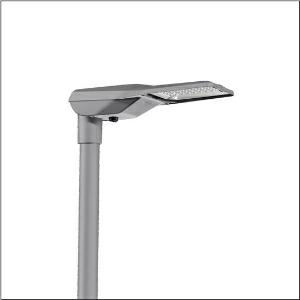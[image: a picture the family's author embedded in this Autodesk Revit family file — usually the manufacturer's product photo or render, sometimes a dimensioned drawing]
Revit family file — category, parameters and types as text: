
# Revit family: streetlight_sl_21_iq_mini___p0_8a_5xe2u31u08gb_cad6
name_source: partatom
category: Lighting Fixtures
units: mm (PartAtom-declared; Revit-internal decimal feet)

## family parameters
Cut with Voids When Loaded = No
Host = Face
Light Source = No
Part Type = Normal
Room Calculation Point = No
Round Connector Dimension = Use Diameter
Shared = No

## types (1)
- --- (1 x LED, 6040 lm, 39.8 W, 3000K)
    Apparent Load = 40 VA
    CIE Flux Codes = 33 69 96 100 100
    Color Rendering = 70
    Color Temperature = 3000K
    Default Elevation = 1800 mm
    Description = Streetlight SL 21 iQ mini, mast luminaire, primary light control with lens, of PMMA, primary optical cover: cover, of toughened safety glass, transparent, light distribution: P0.8a, light emission: direct distribution, primary light characteristic: asymmetric, installation type: post-top, side-entry, LED, High Power LED, rated luminous flux: 6.040lm, luminous efficacy: 152lm/W, light colour: 730, colour temperature: 3000K, control gear: iQ-Street Remote, D4i with power reduction, control: pre-setting: logarithmic dimming characteristic, Street-Remote, Auto-Match, Temp-Guard, Lumen-Switch, Night-Set, Smart-Wire, Light-Fading, Desk-Remote (wireless, voltage-free reading and setting of iQ features in the workshop via application-optimized NFC function/RFID function), optimised constant luminous flux control (CLO 2.0), mains connection: 220..240V, AC, 50/60Hz, start of lifetime: 40W, end of service life: 41W, reduction: 18W, luminaire housing, of diecast aluminium, powder-coated, SITECO metallic grey (DB 702S), corrosivity category C5 high according to DIN EN ISO 12944, please order mast flange separately, inclination adjustable: 0°, 5°, 10°, 15°, sealing non-destructively replaceable, multi-level sealing system, length: 628mm, width: 235mm, height: 110mm, mast flange for spigot size: 42mm (side-entry): 5XC10008XM4, 60/48mm (side-entry/post-top): 5XC10108XM2, 76/60mm (side-entry/post-top): 5XC10108XM1, mounting height: 4..8m, Smart Interface below, protection rating (complete): IP66, insulation class (complete): insulation class II (safety insulation), certification: CE, ENEC, ENEC+, VDE, impact resistance: IK10, permissible operating ambient temperature for outdoor applications: -40..+50°C, standard-compliant lighting for roads and squares, packaging unit: 1 piece

Light Distribution: P0.8a
    Height = 110 mm
    Lamp = 1 x LED
    Lamp Light Flux = 6040 lm
    Lamp Power = 39.8 W
    Lamp count = 1
    Length = 625 mm
    Luminous efficacy = 152 lm/W
    Manufacturer = Siteco
    ModVariant = No
    Model = 5XE2U31U08GB
    Mounting Place = Pole
    Mounting Type = Pole top
    Number of Poles = 1
    OnlyDefault = Yes
    Power Factor = 1
    Product Name = Streetlight SL 21 iQ mini | P0.8a
    Product group = mast luminaire | pylon top
    ProductGroupID = 6100
    Protection Class = Protection class II
    Protection Degree = IP 66
    RLX_Detail_Level = 1
    RLX_Emergency_Light_Flux = 0 lm
    RLX_Emergency_Type = 0
    RLX_Emergency_Type_DB = No
    RlxData = <blob elided: 92501 chars, md5=db89c70b>
    Socket = socket
    Standby Power = 0 W
    System Light Flux = 6040 lm
    System Power = 40 W
    Type Comments = factory setting: luminous flux: 100 % | dim-lin: 254 | 800 mA
    Type Image = l_1003516.jpg
    URL = http://relux.com
    VarID = @adj_083519
    Voltage = 0 V
    Weight = 0.00 kg
    Width = 234 mm

## geometry (parser evidence)
native form markers: Blend x4, Sweep x10
no freeform markers — native parametric forms only
